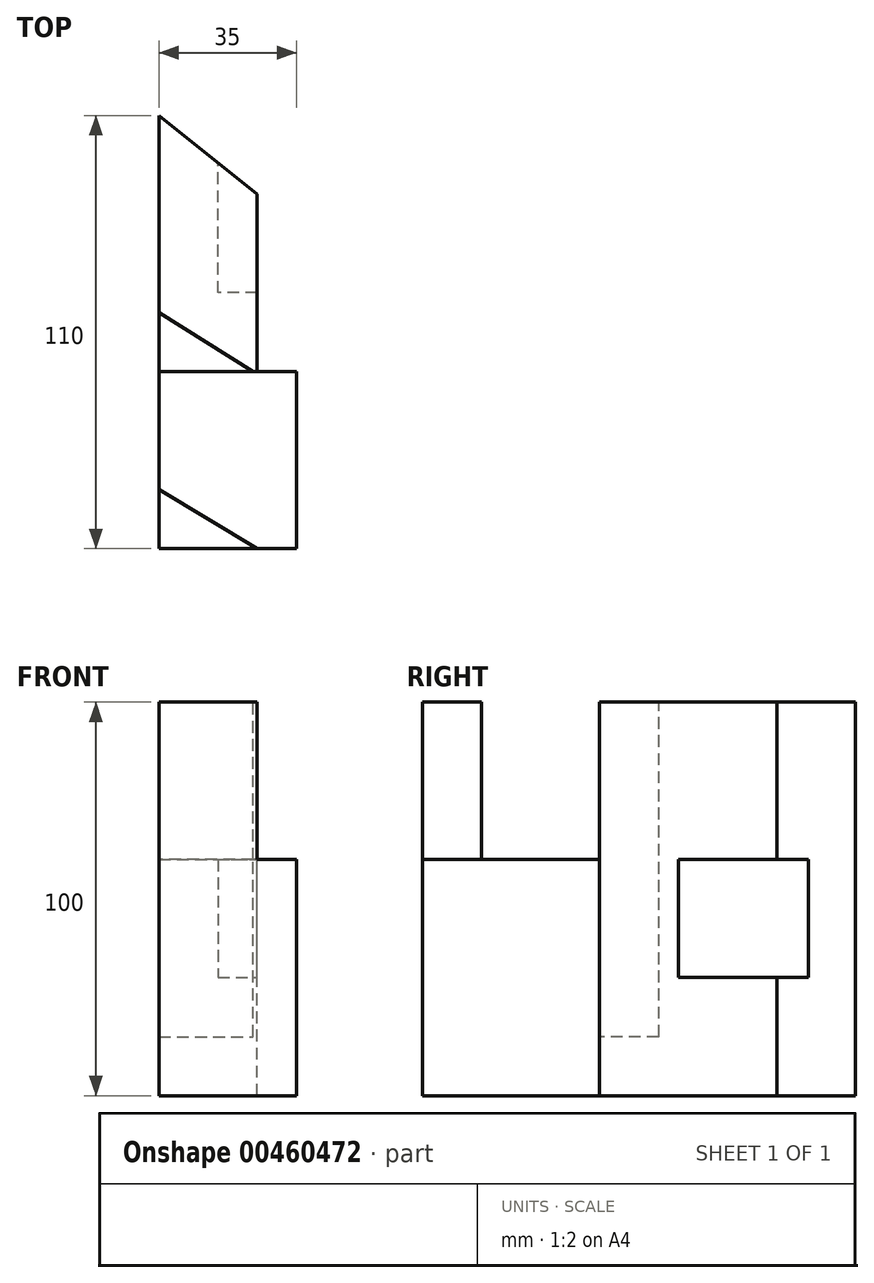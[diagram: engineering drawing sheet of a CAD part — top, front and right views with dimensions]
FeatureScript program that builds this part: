
annotation { "Feature Type Name" : "Feature", "Feature Type Description" : "" }
export const myFeature = defineFeature(function(context is Context, id is Id, definition is map)
    precondition{}
    {
        {
            var Q0;
            Q0=qCreatedBy(makeId("Front.planeOp"),FACE);
            var sketch = newSketch(context, id + "F0", { "sketchPlane" : qUnion([Q0])});
            skLineSegment(sketch, "E0.bottom", {"start": v(0, 0) * mm, "end": v(-35, 0) * mm});
            skLineSegment(sketch, "E0.top", {"start": v(0, 60) * mm, "end": v(-35, 60) * mm});
            skLineSegment(sketch, "E0.left", {"start": v(0, 0) * mm, "end": v(0, 60) * mm});
            skLineSegment(sketch, "E0.right", {"start": v(-35, 0) * mm, "end": v(-35, 60) * mm});
            skSolve(sketch);
        }
        {
            var Q0;
            Q0=makeQuery(id+"F0.imprint","IMPRINT",FACE,{"disambiguationData":[TD([[makeQuery(id+"F0.imprint","IMPRINT",EDGE,{"derivedFrom":sQuery(id+"F0.wireOp",EDGE,"E0.bottom")}),-1.0]])]});
            extrude(context, id + "F1", {"entities" : qUnion([Q0]), "depth" : 45 * mm});
        }
        {
            var Q0;
            Q0=makeQuery(id+"F1.opExtrude","CAP_FACE",FACE,{"disambiguationData":[OSD([sQuery(id+"F0.wireOp",EDGE,"E0.bottom"),sQuery(id+"F0.wireOp",EDGE,"E0.top"),sQuery(id+"F0.wireOp",EDGE,"E0.left"),sQuery(id+"F0.wireOp",EDGE,"E0.right")])],"isStart":true});
            var sketch = newSketch(context, id + "F2", { "sketchPlane" : qUnion([Q0])});
            skLineSegment(sketch, "E1.bottom", {"start": v(35, 0) * mm, "end": v(10, 0) * mm});
            skLineSegment(sketch, "E1.top", {"start": v(35, 100) * mm, "end": v(10, 100) * mm});
            skLineSegment(sketch, "E1.left", {"start": v(35, 0) * mm, "end": v(35, 100) * mm});
            skLineSegment(sketch, "E1.right", {"start": v(10, 0) * mm, "end": v(10, 100) * mm});
            skSolve(sketch);
        }
        {
            var Q0;
            {var subQ0=sQuery(id+"F2.wireOp",EDGE,"E1.top");Q0=makeQuery(id+"F2.imprint","IMPRINT",FACE,{"disambiguationData":[TD([[makeQuery(id+"F2.imprint","IMPRINT",EDGE,{"derivedFrom":subQ0}),1.0]])]});}
            var Q1;
            {var subQ0=sQuery(id+"F2.wireOp",EDGE,"E1.bottom");Q1=makeQuery(id+"F2.imprint","IMPRINT",FACE,{"disambiguationData":[TD([[makeQuery(id+"F2.imprint","IMPRINT",EDGE,{"derivedFrom":subQ0}),1.0]])]});}
            extrude(context, id + "F3", {"entities" : qUnion([Q0, Q1]), "operationType" : NewBodyOperationType.ADD, "depth" : 65 * mm});
        }
        {
            var Q0;
            Q0=makeQuery(id+"F3.opExtrude","CAP_FACE",FACE,{"disambiguationData":[OSD([sQuery(id+"F2.wireOp",EDGE,"E1.bottom"),sQuery(id+"F2.wireOp",EDGE,"E1.top"),sQuery(id+"F2.wireOp",EDGE,"E1.left"),sQuery(id+"F2.wireOp",EDGE,"E1.right")])],"isStart":false});
            var sketch = newSketch(context, id + "F4", { "sketchPlane" : qUnion([Q0])});
            skLineSegment(sketch, "E2", {"start": v(10, 0) * mm, "end": v(10, 30) * mm});
            skLineSegment(sketch, "E3.bottom", {"start": v(10, 30) * mm, "end": v(20, 30) * mm});
            skLineSegment(sketch, "E3.top", {"start": v(10, 60) * mm, "end": v(20, 60) * mm});
            skLineSegment(sketch, "E3.left", {"start": v(10, 30) * mm, "end": v(10, 60) * mm});
            skLineSegment(sketch, "E3.right", {"start": v(20, 30) * mm, "end": v(20, 60) * mm});
            skSolve(sketch);
        }
        {
            var Q0;
            Q0=makeQuery(id+"F4.imprint","IMPRINT",FACE,{"disambiguationData":[TD([[makeQuery(id+"F4.imprint","IMPRINT",EDGE,{"derivedFrom":sQuery(id+"F4.wireOp",EDGE,"E3.bottom")}),1.0]])]});
            extrude(context, id + "F5", {"entities" : qUnion([Q0]), "operationType" : NewBodyOperationType.REMOVE, "oppositeDirection" : true, "depth" : 45 * mm});
        }
        {
            var Q0;
            Q0=makeQuery(id+"F3.opExtrude","SWEPT_FACE",FACE,{"disambiguationData":[OSD([sQuery(id+"F2.wireOp",EDGE,"E1.top")])]});
            var sketch = newSketch(context, id + "F6", { "sketchPlane" : qUnion([Q0])});
            skLineSegment(sketch, "E4", {"start": v(-10, 65) * mm, "end": v(-10, 45) * mm});
            skLineSegment(sketch, "E5", {"start": v(-10, 45) * mm, "end": v(-35, 65) * mm});
            skLineSegment(sketch, "E6", {"start": v(-35, 65) * mm, "end": v(-10, 65) * mm});
            skSolve(sketch);
        }
        {
            var Q0;
            Q0=makeQuery(id+"F6.imprint","IMPRINT",FACE,{"disambiguationData":[TD([[makeQuery(id+"F6.imprint","IMPRINT",EDGE,{"derivedFrom":sQuery(id+"F6.wireOp",EDGE,"E4")}),-1.0]])]});
            extrude(context, id + "F7", {"entities" : qUnion([Q0]), "operationType" : NewBodyOperationType.REMOVE, "oppositeDirection" : true, "depth" : 100 * mm});
        }
        {
            var Q0;
            Q0=makeQuery(id+"F1.opExtrude","SWEPT_FACE",FACE,{"disambiguationData":[OSD([sQuery(id+"F0.wireOp",EDGE,"E0.top")])]});
            var sketch = newSketch(context, id + "F8", { "sketchPlane" : qUnion([Q0])});
            skLineSegment(sketch, "E7", {"start": v(-35, -45) * mm, "end": v(-10, -45) * mm});
            skLineSegment(sketch, "E8", {"start": v(-35, -45) * mm, "end": v(-35, -30) * mm});
            skLineSegment(sketch, "E9", {"start": v(-35, -30) * mm, "end": v(-10, -45) * mm});
            skSolve(sketch);
        }
        {
            var Q0;
            Q0 = qSketchRegion(id + "F8", true);
            extrude(context, id + "F9", {"entities" : qUnion([Q0]), "operationType" : NewBodyOperationType.ADD, "depth" : 40 * mm});
        }
        {
            var Q0;
            Q0=makeQuery(id+"F3.opExtrude","SWEPT_FACE",FACE,{"disambiguationData":[OSD([sQuery(id+"F2.wireOp",EDGE,"E1.top")])]});
            var sketch = newSketch(context, id + "F10", { "sketchPlane" : qUnion([Q0])});
            skLineSegment(sketch, "E10", {"start": v(-35, 0) * mm, "end": v(-11, 0) * mm});
            skLineSegment(sketch, "E11", {"start": v(-35, 0) * mm, "end": v(-35, 15) * mm});
            skLineSegment(sketch, "E12", {"start": v(-35, 15) * mm, "end": v(-11, 0) * mm});
            skSolve(sketch);
        }
        {
            var Q0;
            Q0 = qSketchRegion(id + "F10", true);
            extrude(context, id + "F11", {"entities" : qUnion([Q0]), "operationType" : NewBodyOperationType.REMOVE, "oppositeDirection" : true, "depth" : 85 * mm});
        }
    });
